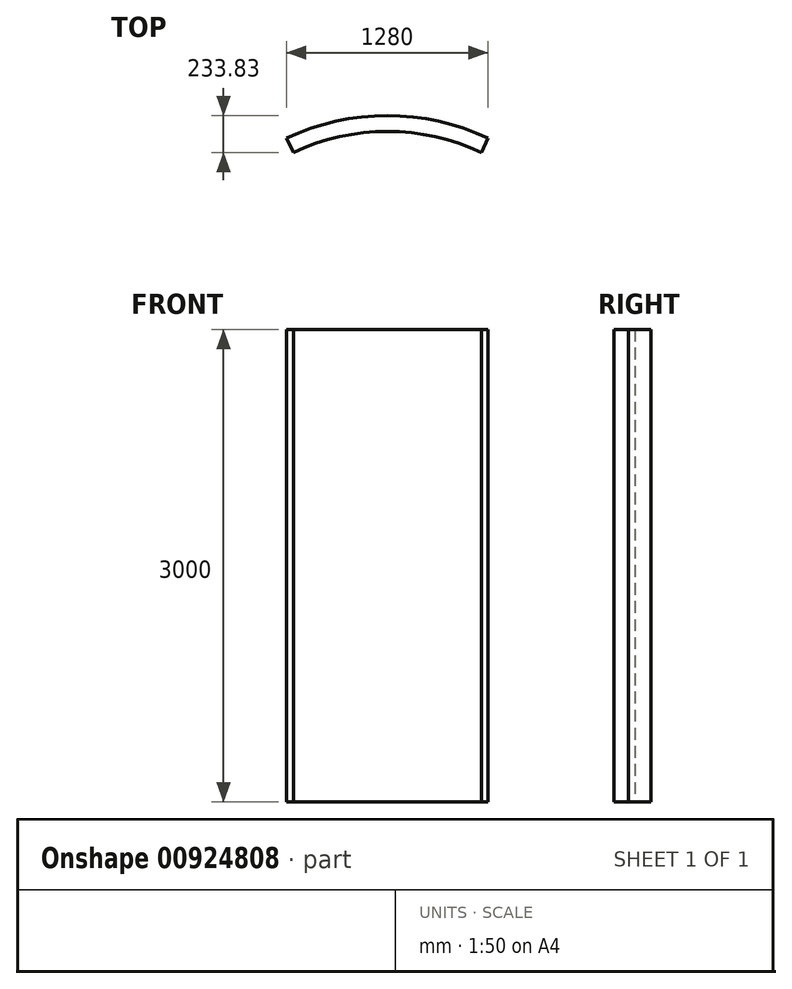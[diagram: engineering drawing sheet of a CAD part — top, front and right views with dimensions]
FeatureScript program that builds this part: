
annotation { "Feature Type Name" : "Feature", "Feature Type Description" : "" }
export const myFeature = defineFeature(function(context is Context, id is Id, definition is map)
    precondition{}
    {
        {
            var Q0;
            Q0=qCreatedBy(makeId("Top.planeOp"),FACE);
            var sketch = newSketch(context, id + "F0", { "sketchPlane" : qUnion([Q0])});
            skArc(sketch, "E0", {"start": v(640, 1356.61) * mm, "mid": v(0, 1500) * mm, "end": v(-640, 1356.61) * mm});
            skArc(sketch, "E1", {"start": v(-597.33, 1266.17) * mm, "mid": v(0, 1400) * mm, "end": v(597.33, 1266.17) * mm});
            skLineSegment(sketch, "E2", {"start": v(597.33, 1266.17) * mm, "end": v(640, 1356.61) * mm});
            skLineSegment(sketch, "E3", {"start": v(-597.33, 1266.17) * mm, "end": v(-640, 1356.61) * mm});
            skSolve(sketch);
        }
        {
            var Q0;
            Q0=makeQuery(id+"F0.imprint","IMPRINT",FACE,{"disambiguationData":[TD([[makeQuery(id+"F0.imprint","IMPRINT",EDGE,{"derivedFrom":sQuery(id+"F0.wireOp",EDGE,"E0")}),1.0]])]});
            extrude(context, id + "F1", {"entities" : qUnion([Q0]), "depth" : 3000 * mm, "offsetDistance" : 25 * mm});
        }
    });
